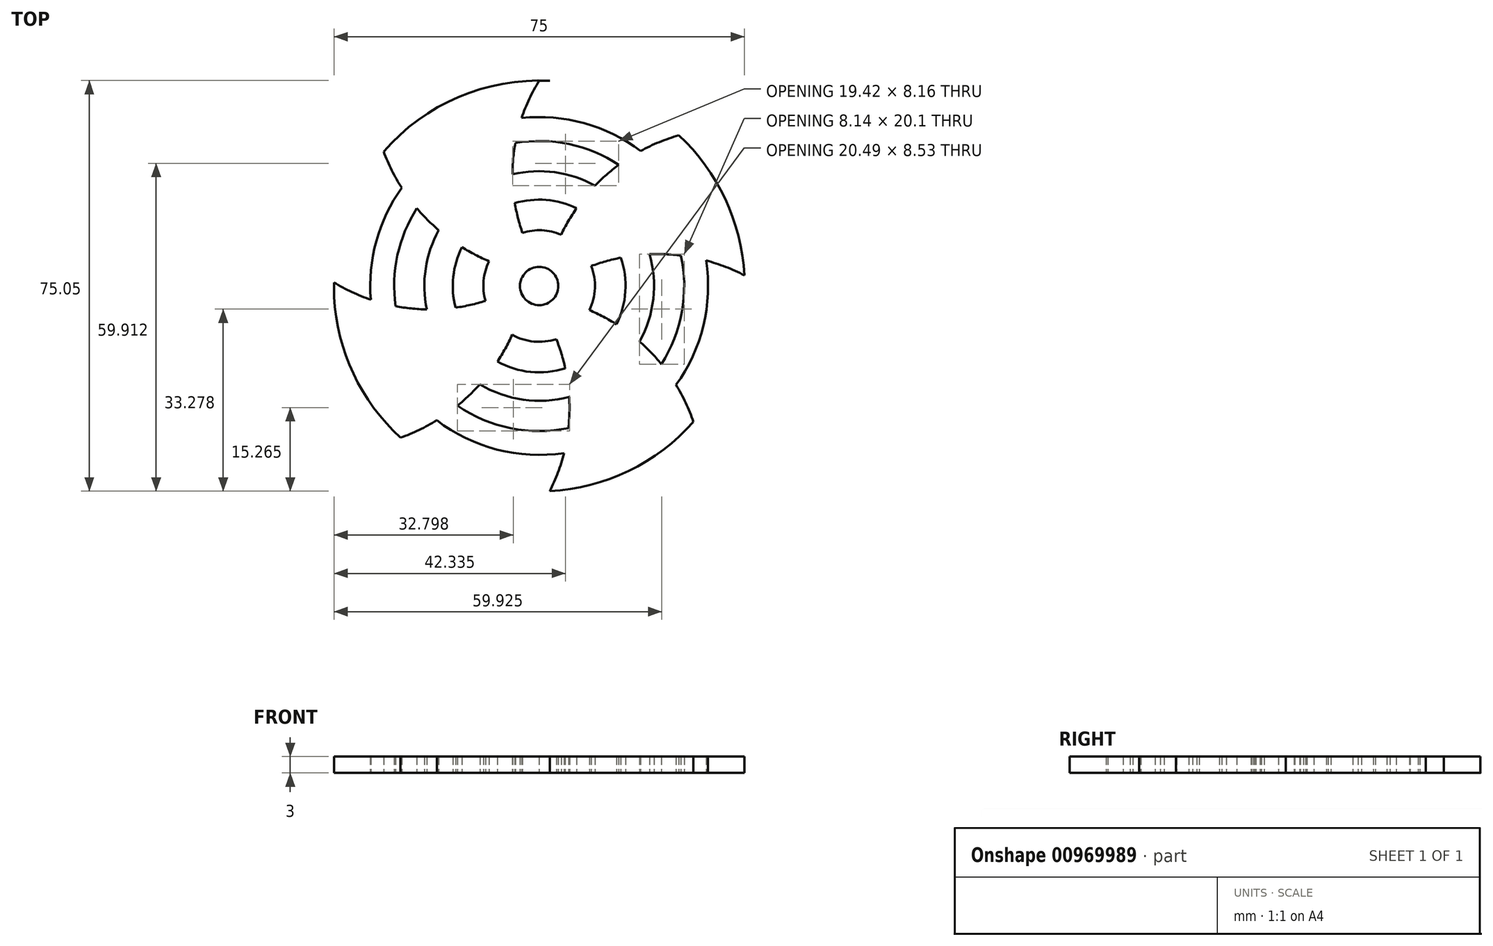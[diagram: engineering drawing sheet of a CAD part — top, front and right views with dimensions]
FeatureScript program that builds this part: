
annotation { "Feature Type Name" : "Feature", "Feature Type Description" : "" }
export const myFeature = defineFeature(function(context is Context, id is Id, definition is map)
    precondition{}
    {
        {
            var Q0;
            Q0=qCreatedBy(makeId("Top.planeOp"),FACE);
            var sketch = newSketch(context, id + "F0", { "sketchPlane" : qUnion([Q0])});
            skLineSegment(sketch, "E0.bottom", {"start": v(-139.43, 50.97) * mm, "end": v(-64.43, 50.97) * mm});
            skLineSegment(sketch, "E0.top", {"start": v(-139.43, -24.03) * mm, "end": v(-64.43, -24.03) * mm});
            skLineSegment(sketch, "E0.left", {"start": v(-139.43, 50.97) * mm, "end": v(-139.43, -24.03) * mm});
            skLineSegment(sketch, "E0.right", {"start": v(-64.43, 50.97) * mm, "end": v(-64.43, -24.03) * mm});
            skPoint(sketch, "E0.middle", {"position": v(-101.93, 13.47) * mm});
            skArc(sketch, "E1", {"start": v(-103.89, -24.03) * mm, "mid": v(-87.36, -21.14) * mm, "end": v(-73.74, -11.34) * mm});
            skCircle(sketch, "E2", {"center": v(-101.93, 13.47) * mm, "radius": 3.5 * mm});
            skArc(sketch, "E3", {"start": v(-101.93, 50.97) * mm, "mid": v(-103.73, 47.66) * mm, "end": v(-105.13, 44.17) * mm});
            skArc(sketch, "E4", {"start": v(-64.43, 15.42) * mm, "mid": v(-67.85, 16.97) * mm, "end": v(-71.42, 18.13) * mm});
            skArc(sketch, "E5", {"start": v(-99.98, -24.03) * mm, "mid": v(-98.5, -20.62) * mm, "end": v(-97.4, -17.07) * mm});
            skArc(sketch, "E6", {"start": v(-139.48, 14.13) * mm, "mid": v(-136.18, 12.36) * mm, "end": v(-132.7, 10.97) * mm});
            skArc(sketch, "E7", {"start": v(-73.74, -11.34) * mm, "mid": v(-75.14, -7.89) * mm, "end": v(-76.9, -4.6) * mm});
            skArc(sketch, "E8", {"start": v(-76.4, 41) * mm, "mid": v(-79.98, 39.77) * mm, "end": v(-83.4, 38.16) * mm});
            skArc(sketch, "E9", {"start": v(-130.36, 38) * mm, "mid": v(-128.88, 34.62) * mm, "end": v(-127.05, 31.42) * mm});
            skArc(sketch, "E10", {"start": v(-127.26, -14.26) * mm, "mid": v(-123.87, -12.84) * mm, "end": v(-120.65, -11.08) * mm});
            skArc(sketch, "E11", {"start": v(-111.07, 17.99) * mm, "mid": v(-112.08, 14.43) * mm, "end": v(-111.75, 10.74) * mm});
            skArc(sketch, "E12", {"start": v(-116.03, 20.55) * mm, "mid": v(-117.63, 15.14) * mm, "end": v(-117.21, 9.51) * mm});
            skArc(sketch, "E13", {"start": v(-120.28, 23.66) * mm, "mid": v(-122.68, 16.62) * mm, "end": v(-122.48, 9.2) * mm});
            skArc(sketch, "E14", {"start": v(-124.3, 27.69) * mm, "mid": v(-127.83, 19.08) * mm, "end": v(-128.17, 9.78) * mm});
            skArc(sketch, "E15", {"start": v(-127.05, 31.42) * mm, "mid": v(-131.69, 21.7) * mm, "end": v(-132.7, 10.97) * mm});
            skPoint(sketch, "E16.orphan", {"position": v(-98.5, 14.13) * mm});
            skPoint(sketch, "E17.orphan", {"position": v(-105.43, 13.47) * mm});
            skArc(sketch, "E18.trimOffspring", {"start": v(-95.1, 27.7) * mm, "mid": v(-100.65, 29.2) * mm, "end": v(-106.37, 28.61) * mm});
            skArc(sketch, "E19.trimOffspring", {"start": v(-91.72, 31.8) * mm, "mid": v(-99.07, 34.26) * mm, "end": v(-106.8, 33.88) * mm});
            skArc(sketch, "E20.trimOffspring", {"start": v(-87.38, 35.62) * mm, "mid": v(-96.46, 39.4) * mm, "end": v(-106.3, 39.6) * mm});
            skArc(sketch, "E21.trimOffspring", {"start": v(-83.4, 38.16) * mm, "mid": v(-93.7, 43.22) * mm, "end": v(-105.13, 44.17) * mm});
            skArc(sketch, "E22.trimOffspring", {"start": v(-95.1, 27.7) * mm, "mid": v(-96.6, 25.33) * mm, "end": v(-97.92, 22.84) * mm});
            skArc(sketch, "E23.trimOffspring", {"start": v(-106.37, 28.61) * mm, "mid": v(-105.8, 25.87) * mm, "end": v(-104.99, 23.2) * mm});
            skArc(sketch, "E24.trimOffspring", {"start": v(-106.3, 39.6) * mm, "mid": v(-106.68, 36.75) * mm, "end": v(-106.8, 33.88) * mm});
            skArc(sketch, "E25.trimOffspring", {"start": v(-87.38, 35.62) * mm, "mid": v(-89.63, 33.8) * mm, "end": v(-91.72, 31.8) * mm});
            skArc(sketch, "E26.trimOffspring", {"start": v(-109.56, -0.35) * mm, "mid": v(-103.49, -2.24) * mm, "end": v(-97.16, -1.58) * mm});
            skArc(sketch, "E27.trimOffspring", {"start": v(-112.77, -4.5) * mm, "mid": v(-104.84, -7.31) * mm, "end": v(-96.45, -6.79) * mm});
            skArc(sketch, "E28.trimOffspring", {"start": v(-116.88, -8.41) * mm, "mid": v(-107.14, -12.51) * mm, "end": v(-96.58, -12.48) * mm});
            skArc(sketch, "E29.trimOffspring", {"start": v(-120.65, -11.08) * mm, "mid": v(-109.63, -16.43) * mm, "end": v(-97.4, -17.07) * mm});
            skArc(sketch, "E30.trimOffspring", {"start": v(-87.8, 6.46) * mm, "mid": v(-86.18, 12.47) * mm, "end": v(-87.02, 18.64) * mm});
            skArc(sketch, "E31.trimOffspring", {"start": v(-83.57, 3.3) * mm, "mid": v(-81.08, 11.1) * mm, "end": v(-81.76, 19.27) * mm});
            skArc(sketch, "E32.trimOffspring", {"start": v(-79.6, -0.8) * mm, "mid": v(-75.85, 8.76) * mm, "end": v(-76.02, 19.03) * mm});
            skArc(sketch, "E33.trimOffspring", {"start": v(-76.9, -4.6) * mm, "mid": v(-71.92, 6.22) * mm, "end": v(-71.42, 18.13) * mm});
            skArc(sketch, "E34.trimOffspring", {"start": v(-116.03, 20.55) * mm, "mid": v(-113.6, 19.17) * mm, "end": v(-111.07, 17.99) * mm});
            skArc(sketch, "E35.trimOffspring", {"start": v(-117.21, 9.51) * mm, "mid": v(-114.46, 10.02) * mm, "end": v(-111.75, 10.74) * mm});
            skArc(sketch, "E36.trimOffspring", {"start": v(-109.56, -0.35) * mm, "mid": v(-108.11, 2.05) * mm, "end": v(-106.86, 4.54) * mm});
            skArc(sketch, "E37.trimOffspring", {"start": v(-97.16, -1.58) * mm, "mid": v(-97.87, 1.13) * mm, "end": v(-98.8, 3.77) * mm});
            skArc(sketch, "E38.trimOffspring", {"start": v(-87.8, 6.46) * mm, "mid": v(-90.21, 7.86) * mm, "end": v(-92.74, 9.06) * mm});
            skArc(sketch, "E39.trimOffspring", {"start": v(-87.02, 18.64) * mm, "mid": v(-89.75, 17.99) * mm, "end": v(-92.41, 17.12) * mm});
            skArc(sketch, "E40.trimOffspring", {"start": v(-76.02, 19.03) * mm, "mid": v(-78.89, 19.27) * mm, "end": v(-81.76, 19.27) * mm});
            skArc(sketch, "E41.trimOffspring", {"start": v(-79.6, -0.8) * mm, "mid": v(-81.5, 1.33) * mm, "end": v(-83.57, 3.3) * mm});
            skArc(sketch, "E42.trimOffspring", {"start": v(-96.58, -12.48) * mm, "mid": v(-96.4, -9.64) * mm, "end": v(-96.45, -6.79) * mm});
            skArc(sketch, "E43.trimOffspring", {"start": v(-116.88, -8.41) * mm, "mid": v(-114.75, -6.54) * mm, "end": v(-112.77, -4.5) * mm});
            skArc(sketch, "E44.trimOffspring", {"start": v(-128.17, 9.78) * mm, "mid": v(-125.34, 9.37) * mm, "end": v(-122.48, 9.2) * mm});
            skArc(sketch, "E45.trimOffspring", {"start": v(-124.3, 27.69) * mm, "mid": v(-122.37, 25.59) * mm, "end": v(-120.28, 23.66) * mm});
            skArc(sketch, "E46.trimOffspring", {"start": v(-97.92, 22.84) * mm, "mid": v(-101.42, 23.65) * mm, "end": v(-104.99, 23.2) * mm});
            skArc(sketch, "E47.trimOffspring", {"start": v(-92.74, 9.06) * mm, "mid": v(-91.75, 13.05) * mm, "end": v(-92.41, 17.12) * mm});
            skArc(sketch, "E48.trimOffspring", {"start": v(-106.86, 4.54) * mm, "mid": v(-102.9, 3.32) * mm, "end": v(-98.8, 3.77) * mm});
            skArc(sketch, "E49.trimOffspring", {"start": v(-139.43, 15.42) * mm, "mid": v(-136.67, -0.78) * mm, "end": v(-127.26, -14.26) * mm});
            skArc(sketch, "E50.trimOffspring", {"start": v(-99.98, 50.97) * mm, "mid": v(-116.67, 48) * mm, "end": v(-130.36, 38) * mm});
            skArc(sketch, "E51.trimOffspring", {"start": v(-64.43, 11.51) * mm, "mid": v(-67.14, 27.59) * mm, "end": v(-76.4, 41) * mm});
            skSolve(sketch);
        }
        {
            var Q0;
            {var subQ0=sQuery(id+"F0.wireOp",EDGE,"E0.bottom");var subQ1=makeQuery(id+"F0.imprint","INTERSECT",VERTEX,{"derivedFrom":[subQ0,sQuery(id+"F0.wireOp",EDGE,"E3")]});Q0=makeQuery(id+"F0.imprint","IMPRINT",FACE,{"disambiguationData":[TD([[makeQuery(id+"F0.imprint","IMPRINT",EDGE,{"disambiguationData":[TD([[subQ1,1.0]])],"derivedFrom":subQ0}),1.0]])]});}
            var Q1;
            {var subQ0=sQuery(id+"F0.wireOp",EDGE,"E1");var subQ1=sQuery(id+"F0.wireOp",EDGE,"E0.left");var subQ2=makeQuery(id+"F0.imprint","INTERSECT",VERTEX,{"disambiguationData":[OD(0.0)],"derivedFrom":[subQ1,subQ0]});Q1=makeQuery(id+"F0.imprint","IMPRINT",FACE,{"disambiguationData":[TD([[makeQuery(id+"F0.imprint","IMPRINT",EDGE,{"disambiguationData":[TD([[subQ2,-1.0]])],"derivedFrom":subQ1}),-1.0]])]});}
            var Q2;
            {var subQ0=sQuery(id+"F0.wireOp",EDGE,"E1");var subQ1=sQuery(id+"F0.wireOp",EDGE,"E0.left");var subQ2=makeQuery(id+"F0.imprint","INTERSECT",VERTEX,{"disambiguationData":[OD(1.0)],"derivedFrom":[subQ1,subQ0]});Q2=makeQuery(id+"F0.imprint","IMPRINT",FACE,{"disambiguationData":[TD([[makeQuery(id+"F0.imprint","IMPRINT",EDGE,{"disambiguationData":[TD([[subQ2,1.0]])],"derivedFrom":subQ1}),-1.0]])]});}
            var Q3;
            Q3=makeQuery(id+"F0.imprint","IMPRINT",FACE,{"disambiguationData":[TD([[makeQuery(id+"F0.imprint","IMPRINT",EDGE,{"derivedFrom":sQuery(id+"F0.wireOp",EDGE,"E2")}),-1.0]])]});
            extrude(context, id + "F1", {"entities" : qUnion([Q0, Q1, Q2, Q3]), "depth" : 3 * mm, "offsetDistance" : 25 * mm});
        }
    });
